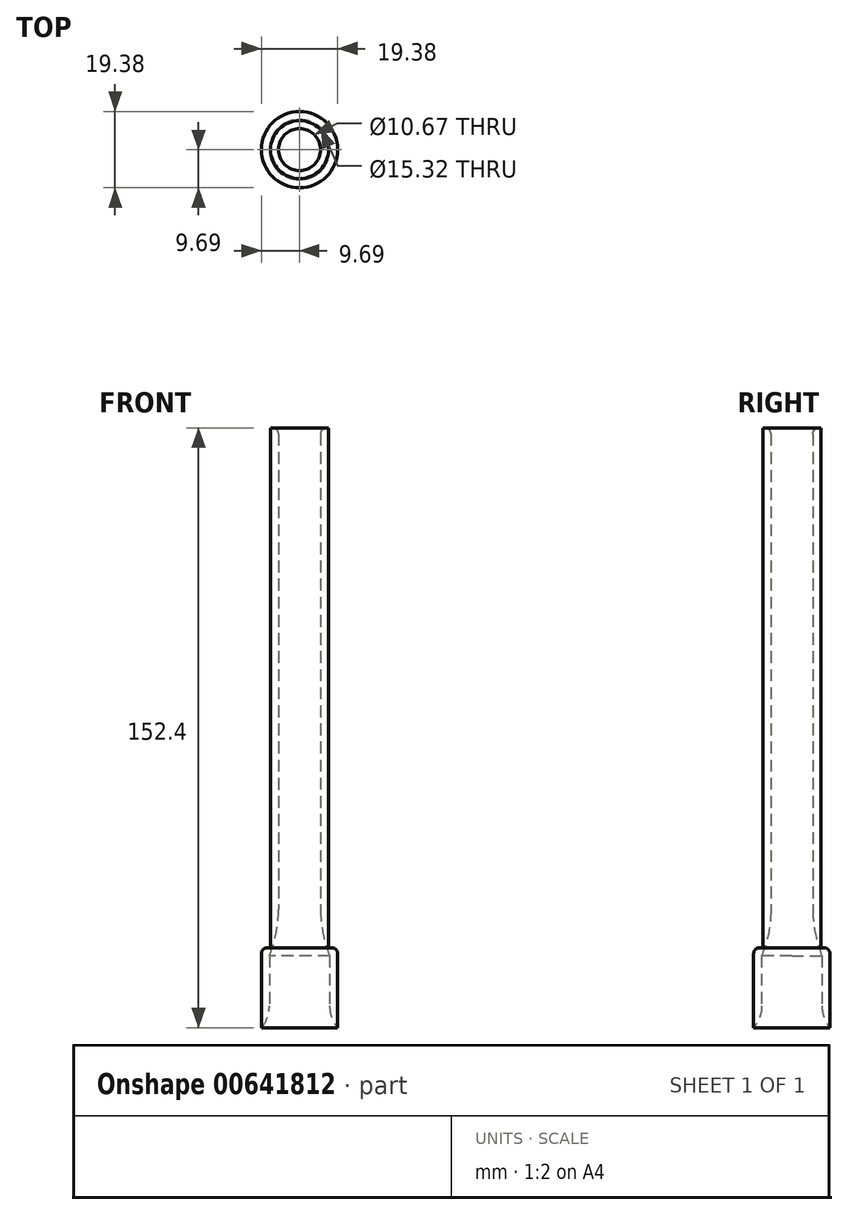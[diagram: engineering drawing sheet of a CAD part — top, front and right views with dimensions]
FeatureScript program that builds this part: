
annotation { "Feature Type Name" : "Feature", "Feature Type Description" : "" }
export const myFeature = defineFeature(function(context is Context, id is Id, definition is map)
    precondition{}
    {
        {
            var Q0;
            Q0=qCreatedBy(makeId("Top.planeOp"),FACE);
            var sketch = newSketch(context, id + "F0", { "sketchPlane" : qUnion([Q0])});
            skCircle(sketch, "E0", {"center": v(0, 0) * mm, "radius": 7.37 * mm});
            skSolve(sketch);
        }
        {
            var Q0;
            Q0=makeQuery(id+"F0.imprint","IMPRINT",FACE,{"disambiguationData":[TD([[makeQuery(id+"F0.imprint","IMPRINT",EDGE,{"derivedFrom":sQuery(id+"F0.wireOp",EDGE,"E0")}),1.0]])]});
            extrude(context, id + "F1", {"entities" : qUnion([Q0]), "depth" : 152.4 * mm, "offsetDistance" : 25.4 * mm});
        }
        {
            var Q0;
            Q0=makeQuery(id+"F1.opExtrude","CAP_FACE",FACE,{"disambiguationData":[OSD([sQuery(id+"F0.wireOp",EDGE,"E0")])],"isStart":false});
            var Q1;
            Q1=makeQuery(id+"F1.opExtrude","CAP_FACE",FACE,{"disambiguationData":[OSD([sQuery(id+"F0.wireOp",EDGE,"E0")])],"isStart":true});
            shell(context, id + "F2", {"entities" : qUnion([Q0, Q1]), "thickness" : 2.03 * mm});
        }
        {
            var Q0;
            Q0=qCreatedBy(makeId("Top.planeOp"),FACE);
            var sketch = newSketch(context, id + "F3", { "sketchPlane" : qUnion([Q0])});
            skCircle(sketch, "E1", {"center": v(0, 0) * mm, "radius": 9.7 * mm});
            skSolve(sketch);
        }
        {
            var Q0;
            Q0 = qSketchRegion(id + "F3", true);
            extrude(context, id + "F4", {"entities" : qUnion([Q0]), "operationType" : NewBodyOperationType.ADD, "depth" : 20.32 * mm, "offsetDistance" : 25.4 * mm});
        }
        {
            var Q0;
            Q0=makeQuery(id+"F4.boolean.opBoolean","MERGE",FACE,{"derivedFrom":[makeQuery(id+"F1.opExtrude","CAP_FACE",FACE,{"disambiguationData":[OSD([sQuery(id+"F0.wireOp",EDGE,"E0")])],"isStart":true}),makeQuery(id+"F4.opExtrude","CAP_FACE",FACE,{"disambiguationData":[OSD([sQuery(id+"F3.wireOp",EDGE,"E1")])],"isStart":true})]});
            var Q1;
            Q1=makeQuery(id+"F4.boolean.opBoolean","SPLIT",FACE,{"disambiguationData":[TD([makeQuery(id+"F2.opShell","OFFSET_FACE",FACE,{"disambiguationData":[OSD([sQuery(id+"F0.wireOp",EDGE,"E0")])]})])],"derivedFrom":makeQuery(id+"F4.opExtrude","CAP_FACE",FACE,{"disambiguationData":[OSD([sQuery(id+"F3.wireOp",EDGE,"E1")])],"isStart":false})});
            shell(context, id + "F5", {"entities" : qUnion([Q0, Q1]), "thickness" : 2.03 * mm});
        }
        {
            var Q0;
            Q0=makeQuery(id+"F5.opShell","OFFSET_EDGE",EDGE,{"disambiguationData":[OSD([sQuery(id+"F0.wireOp",EDGE,"E0"),sQuery(id+"F3.wireOp",EDGE,"E1")])]});
            fillet(context, id + "F6", {"entities" : qUnion([Q0]), "radius" : 30.66 * mm, "tangentPropagation" : true, "allowEdgeOverflow" : false});
        }
        {
            var Q0;
            Q0=makeQuery(id+"F4.opExtrude","CAP_EDGE",EDGE,{"disambiguationData":[OSD([sQuery(id+"F3.wireOp",EDGE,"E1")])],"isStart":false});
            fillet(context, id + "F7", {"entities" : qUnion([Q0]), "radius" : 1.52 * mm, "tangentPropagation" : true, "allowEdgeOverflow" : false});
        }
        {
            var Q0;
            {var subQ0=sQuery(id+"F0.wireOp",EDGE,"E0");Q0=makeQuery(id+"F2.opShell","OFFSET_EDGE",EDGE,{"disambiguationData":[OSD([subQ0]),TDD([makeQuery(id+"F1.opExtrude","CAP_EDGE",EDGE,{"disambiguationData":[OSD([subQ0])],"isStart":false})])]});}
            fillet(context, id + "F8", {"entities" : qUnion([Q0]), "radius" : 1.53 * mm, "tangentPropagation" : true, "allowEdgeOverflow" : false});
        }
        {
            var Q0;
            {var subQ0=sQuery(id+"F3.wireOp",EDGE,"E1");Q0=makeQuery(id+"F5.opShell","OFFSET_EDGE",EDGE,{"disambiguationData":[OSD([subQ0]),TDD([makeQuery(id+"F4.opExtrude","CAP_EDGE",EDGE,{"disambiguationData":[OSD([subQ0])],"isStart":true})])]});}
            fillet(context, id + "F9", {"entities" : qUnion([Q0]), "radius" : 8.46 * mm, "tangentPropagation" : true, "allowEdgeOverflow" : false});
        }
    });
